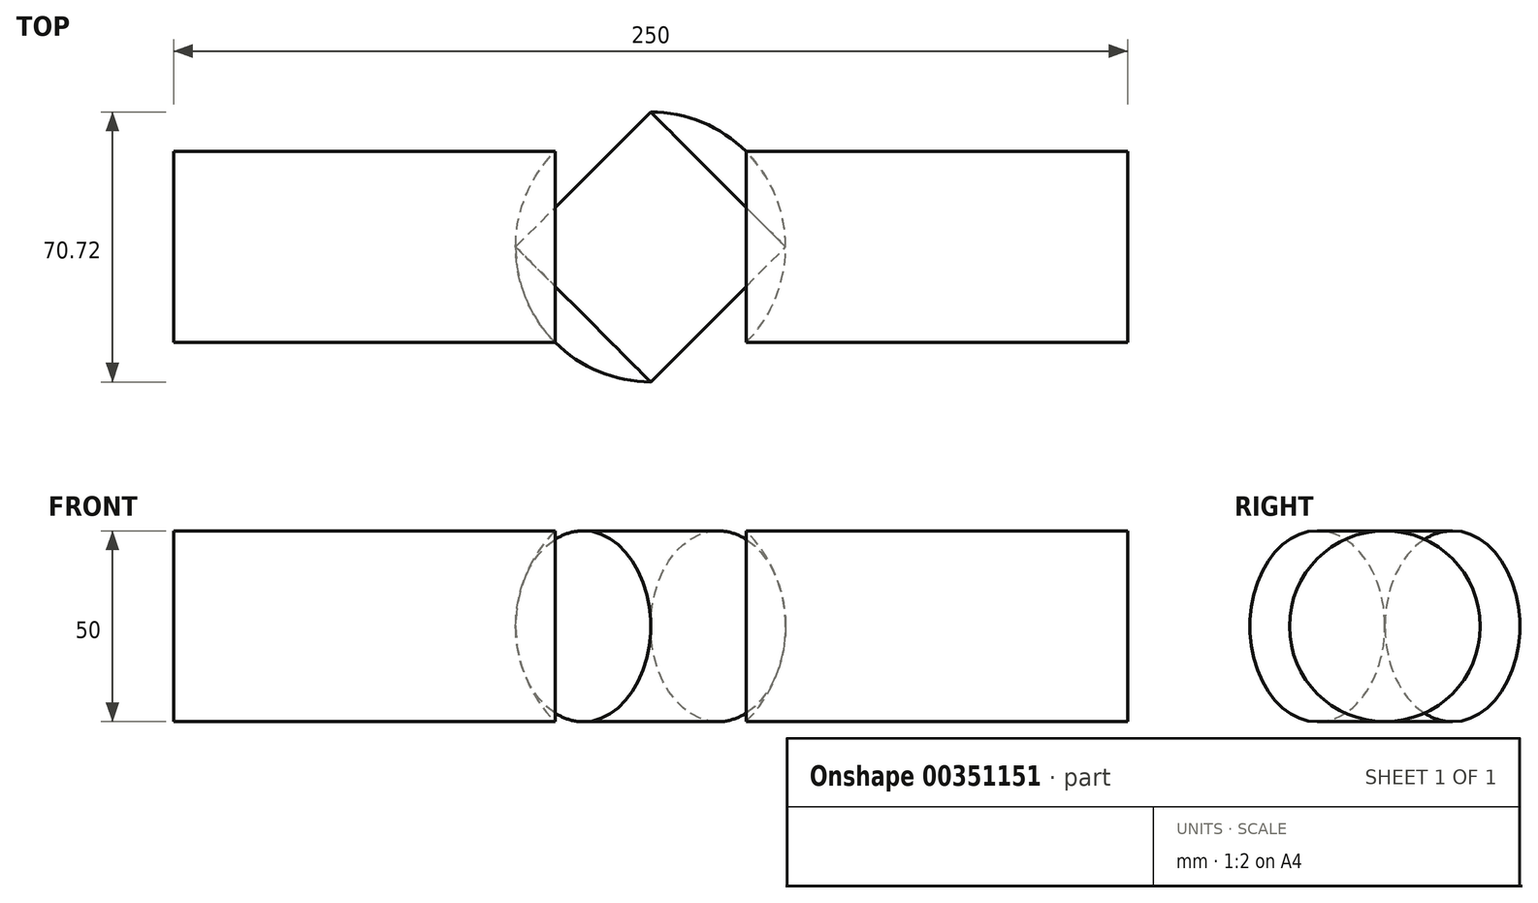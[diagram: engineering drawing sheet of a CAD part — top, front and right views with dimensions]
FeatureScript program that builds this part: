
annotation { "Feature Type Name" : "Feature", "Feature Type Description" : "" }
export const myFeature = defineFeature(function(context is Context, id is Id, definition is map)
    precondition{}
    {
        {
            var Q0;
            Q0=qCreatedBy(makeId("Top.planeOp"),FACE);
            var sketch = newSketch(context, id + "F0", { "sketchPlane" : qUnion([Q0])});
            skLineSegment(sketch, "E0", {"start": v(-25, 0) * mm, "end": v(-25, 25) * mm});
            skLineSegment(sketch, "E1", {"start": v(-25, 25) * mm, "end": v(25, 25) * mm});
            skLineSegment(sketch, "E2", {"start": v(25, 25) * mm, "end": v(25, 0) * mm});
            skLineSegment(sketch, "E3", {"start": v(25, 0) * mm, "end": v(-25, 0) * mm});
            skCircle(sketch, "E4", {"center": v(0, 0) * mm, "radius": 35.36 * mm});
            skLineSegment(sketch, "E5", {"start": v(-25, 0) * mm, "end": v(-125, 0) * mm});
            skLineSegment(sketch, "E6", {"start": v(-125, 0) * mm, "end": v(-125, 25) * mm});
            skLineSegment(sketch, "E7", {"start": v(-125, 25) * mm, "end": v(-25, 25) * mm});
            skLineSegment(sketch, "E8", {"start": v(25, 0) * mm, "end": v(125, 0) * mm});
            skLineSegment(sketch, "E9", {"start": v(125, 0) * mm, "end": v(125, 25) * mm});
            skLineSegment(sketch, "E10", {"start": v(125, 25) * mm, "end": v(25, 25) * mm});
            skLineSegment(sketch, "E11", {"start": v(0, -42.4) * mm, "end": v(0, 45.57) * mm, "construction": true});
            skSolve(sketch);
        }
        {
            var Q0;
            {var subQ4=sQuery(id+"F0.wireOp",EDGE,"E6");Q0=makeQuery(id+"F0.imprint","IMPRINT",FACE,{"disambiguationData":[TD([[makeQuery(id+"F0.imprint","IMPRINT",EDGE,{"derivedFrom":subQ4}),-1.0]])]});}
            var Q1;
            {var subQ4=sQuery(id+"F0.wireOp",EDGE,"E9");Q1=makeQuery(id+"F0.imprint","IMPRINT",FACE,{"disambiguationData":[TD([[makeQuery(id+"F0.imprint","IMPRINT",EDGE,{"derivedFrom":subQ4}),1.0]])]});}
            var Q2;
            Q2=sQuery(id+"F0.wireOp",EDGE,"E3");
            revolve(context, id + "F1", {"entities" : qUnion([Q0, Q1]), "axis" : qUnion([Q2]), "revolveType" : RevolveType.FULL});
        }
        {
            var Q0;
            Q0=makeQuery(id+"F0.imprint","IMPRINT",FACE,{"disambiguationData":[TD([[makeQuery(id+"F0.imprint","IMPRINT",EDGE,{"derivedFrom":sQuery(id+"F0.wireOp",EDGE,"E0")}),-1.0]])]});
            var Q1;
            {var subQ0=sQuery(id+"F0.wireOp",EDGE,"E0");Q1=makeQuery(id+"F0.imprint","IMPRINT",FACE,{"disambiguationData":[TD([[makeQuery(id+"F0.imprint","IMPRINT",EDGE,{"derivedFrom":subQ0}),1.0]])]});}
            var Q2;
            {var subQ0=sQuery(id+"F0.wireOp",EDGE,"E2");Q2=makeQuery(id+"F0.imprint","IMPRINT",FACE,{"disambiguationData":[TD([[makeQuery(id+"F0.imprint","IMPRINT",EDGE,{"derivedFrom":subQ0}),1.0]])]});}
            var Q3;
            Q3=sQuery(id+"F0.wireOp",EDGE,"E3");
            revolve(context, id + "F2", {"entities" : qUnion([Q0, Q1, Q2]), "axis" : qUnion([Q3]), "revolveType" : RevolveType.FULL});
        }
        {
            var Q0;
            Q0=qCreatedBy(makeId("Right.planeOp"),FACE);
            var sketch = newSketch(context, id + "F3", { "sketchPlane" : qUnion([Q0])});
            skLineSegment(sketch, "E12", {"start": v(0, 0) * mm, "end": v(0, 56.86) * mm, "construction": true});
            skSolve(sketch);
        }
        {
            var Q0;
            Q0=makeQuery(id+"F2.opRevolve","SWEPT_BODY",BODY,{"disambiguationData":[OSD([sQuery(id+"F0.wireOp",EDGE,"E1"),sQuery(id+"F0.wireOp",EDGE,"E3"),sQuery(id+"F0.wireOp",EDGE,"E4"),sQuery(id+"F0.wireOp",EDGE,"E5"),sQuery(id+"F0.wireOp",EDGE,"E8")])]});
            var Q1;
            Q1=sQuery(id+"F3.wireOp",EDGE,"E12");
            transform(context, id + "F4", {"entities" : qUnion([Q0]), "transformType" : TransformType.ROTATION, "transformAxis" : qUnion([Q1]), "angle" : 45 * degree, "makeCopy" : false});
        }
    });
